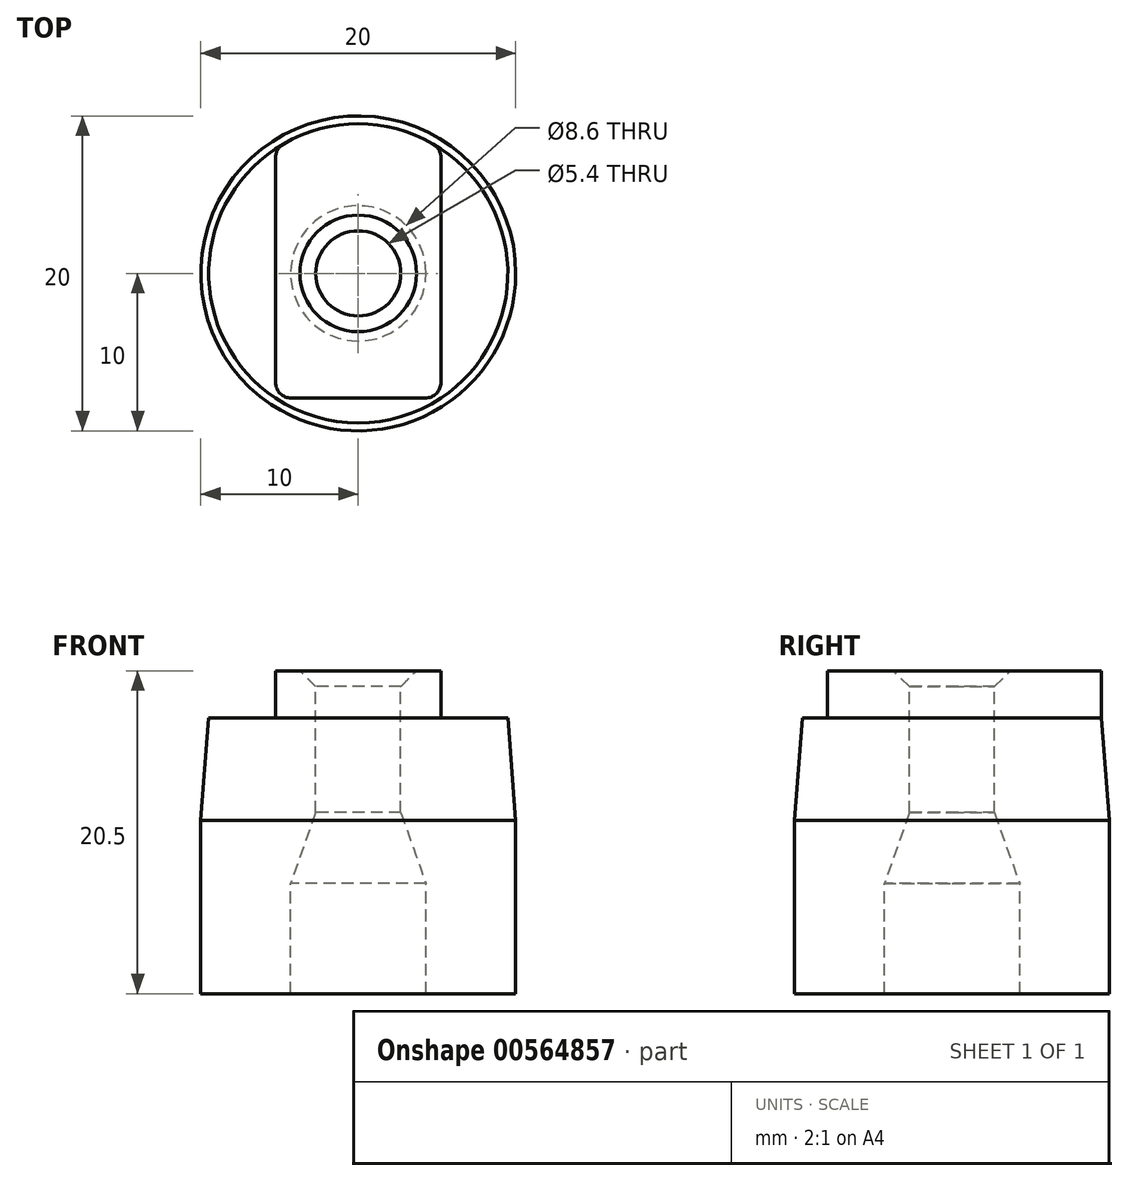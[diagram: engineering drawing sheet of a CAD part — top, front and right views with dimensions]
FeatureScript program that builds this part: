
annotation { "Feature Type Name" : "Feature", "Feature Type Description" : "" }
export const myFeature = defineFeature(function(context is Context, id is Id, definition is map)
    precondition{}
    {
        {
            var Q0;
            Q0=qCreatedBy(makeId("Front.planeOp"),FACE);
            var sketch = newSketch(context, id + "F0", { "sketchPlane" : qUnion([Q0])});
            skLineSegment(sketch, "E0", {"start": v(4.3, 0) * mm, "end": v(10, 0) * mm});
            skLineSegment(sketch, "E1", {"start": v(10, 0) * mm, "end": v(10, 11) * mm});
            skLineSegment(sketch, "E2", {"start": v(10, 11) * mm, "end": v(9.5, 17.5) * mm});
            skLineSegment(sketch, "E3", {"start": v(9.5, 17.5) * mm, "end": v(2.7, 17.5) * mm});
            skLineSegment(sketch, "E4", {"start": v(2.7, 17.5) * mm, "end": v(2.7, 11.5) * mm});
            skLineSegment(sketch, "E5", {"start": v(2.7, 11.5) * mm, "end": v(4.3, 7) * mm});
            skLineSegment(sketch, "E6", {"start": v(4.3, 7) * mm, "end": v(4.3, 0) * mm});
            skSolve(sketch);
        }
        {
            var Q0;
            Q0=qCreatedBy(makeId("Front.planeOp"),FACE);
            var sketch = newSketch(context, id + "F1", { "sketchPlane" : qUnion([Q0])});
            skLineSegment(sketch, "E7", {"start": v(0, 48.35) * mm, "end": v(0, -22.75) * mm});
            skSolve(sketch);
        }
        {
            var Q0;
            Q0=qSketchRegion(id+"F0",true);
            var Q1;
            Q1=sQuery(id+"F1.wireOp",EDGE,"E7");
            revolve(context, id + "F2", {"entities" : qUnion([Q0]), "axis" : qUnion([Q1]), "revolveType" : RevolveType.FULL});
        }
        {
            var Q0;
            Q0=makeQuery(id+"F2.opRevolve","SWEPT_FACE",FACE,{"disambiguationData":[OSD([sQuery(id+"F0.wireOp",EDGE,"E3")])]});
            var sketch = newSketch(context, id + "F3", { "sketchPlane" : qUnion([Q0])});
            skLineSegment(sketch, "E8.bottom", {"start": v(5.25, 7.92) * mm, "end": v(-5.25, 7.92) * mm});
            skLineSegment(sketch, "E8.top", {"start": v(5.25, -7.92) * mm, "end": v(-5.25, -7.92) * mm});
            skLineSegment(sketch, "E8.left", {"start": v(5.25, 7.92) * mm, "end": v(5.25, -7.92) * mm});
            skLineSegment(sketch, "E8.right", {"start": v(-5.25, 7.92) * mm, "end": v(-5.25, -7.92) * mm});
            skPoint(sketch, "E8.middle", {"position": v(0, 0) * mm});
            skSolve(sketch);
        }
        {
            var Q0;
            Q0=makeQuery(id+"F3.imprint","IMPRINT",FACE,{"disambiguationData":[TD([[makeQuery(id+"F3.imprint","IMPRINT",EDGE,{"derivedFrom":sQuery(id+"F3.wireOp",EDGE,"E8.bottom")}),1.0]])]});
            extrude(context, id + "F4", {"entities" : qUnion([Q0]), "operationType" : NewBodyOperationType.ADD, "depth" : 3 * mm});
        }
        {
            var Q0;
            Q0=makeQuery(id+"F4.opExtrude","SWEPT_EDGE",EDGE,{"disambiguationData":[OSD([sQuery(id+"F3.wireOp",EDGE,"E8.top"),sQuery(id+"F3.wireOp",EDGE,"E8.right")])]});
            var Q1;
            Q1=makeQuery(id+"F4.opExtrude","SWEPT_EDGE",EDGE,{"disambiguationData":[OSD([sQuery(id+"F3.wireOp",EDGE,"E8.top"),sQuery(id+"F3.wireOp",EDGE,"E8.left")])]});
            fillet(context, id + "F5", {"entities" : qUnion([Q0, Q1]), "radius" : 1 * mm, "allowEdgeOverflow" : false});
        }
        {
            var Q0;
            {var subQ0=makeQuery(id+"F2.opRevolve","SWEPT_FACE",FACE,{"disambiguationData":[OSD([sQuery(id+"F0.wireOp",EDGE,"E3")])]});Q0=makeQuery(id+"F4.boolean.opBoolean","SPLIT",FACE,{"disambiguationData":[TD([makeQuery(id+"F2.opRevolve","SWEPT_FACE",FACE,{"disambiguationData":[OSD([sQuery(id+"F0.wireOp",EDGE,"E2")])]}),subQ0,makeQuery(id+"F4.opExtrude","SWEPT_FACE",FACE,{"disambiguationData":[OSD([sQuery(id+"F3.wireOp",EDGE,"E8.bottom")])]}),makeQuery(id+"F4.opExtrude","SWEPT_FACE",FACE,{"disambiguationData":[OSD([sQuery(id+"F3.wireOp",EDGE,"E8.left")])]}),makeQuery(id+"F4.opExtrude","SWEPT_FACE",FACE,{"disambiguationData":[OSD([sQuery(id+"F3.wireOp",EDGE,"E8.right")])]})])],"derivedFrom":subQ0});}
            var sketch = newSketch(context, id + "F6", { "sketchPlane" : qUnion([Q0])});
            skLineSegment(sketch, "E9", {"start": v(5.25, 7.92) * mm, "end": v(-5.25, 7.92) * mm});
            skArc(sketch, "E10", {"start": v(5.25, 7.92) * mm, "mid": v(0, 9.5) * mm, "end": v(-5.25, 7.92) * mm});
            skSolve(sketch);
        }
        {
            var Q0;
            Q0=qSketchRegion(id+"F6",true);
            extrude(context, id + "F7", {"entities" : qUnion([Q0]), "operationType" : NewBodyOperationType.ADD, "depth" : 3 * mm});
        }
        {
            var Q0;
            {var subQ0=sQuery(id+"F6.wireOp",EDGE,"E10");var subQ1=sQuery(id+"F6.wireOp",EDGE,"E9");var subQ2=sQuery(id+"F0.wireOp",EDGE,"E3");var subQ3=sQuery(id+"F0.wireOp",EDGE,"E2");Q0=makeQuery(id+"F7.boolean.opBoolean","MERGE",EDGE,{"derivedFrom":[makeQuery(id+"F4.opExtrude","SWEPT_EDGE",EDGE,{"disambiguationData":[OSD([subQ3,subQ2,sQuery(id+"F3.wireOp",EDGE,"E8.bottom"),sQuery(id+"F3.wireOp",EDGE,"E8.right")])]}),makeQuery(id+"F7.opExtrude","SWEPT_EDGE",EDGE,{"disambiguationData":[OSD([subQ3,subQ2,subQ1,subQ0]),TDD([makeQuery(id+"F6.imprint","INTERSECT",VERTEX,{"disambiguationData":[OD(1.0)],"derivedFrom":[makeQuery(id+"F4.boolean.opBoolean","SPLIT",EDGE,{"disambiguationData":[OD(0.0)],"derivedFrom":makeQuery(id+"F2.opRevolve","SWEPT_EDGE",EDGE,{"disambiguationData":[OSD([subQ3,subQ2])]})}),subQ1,subQ0]})])]})]});}
            var Q1;
            {var subQ0=sQuery(id+"F6.wireOp",EDGE,"E10");var subQ1=sQuery(id+"F6.wireOp",EDGE,"E9");var subQ2=sQuery(id+"F0.wireOp",EDGE,"E3");var subQ3=sQuery(id+"F0.wireOp",EDGE,"E2");Q1=makeQuery(id+"F7.boolean.opBoolean","MERGE",EDGE,{"derivedFrom":[makeQuery(id+"F4.opExtrude","SWEPT_EDGE",EDGE,{"disambiguationData":[OSD([subQ3,subQ2,sQuery(id+"F3.wireOp",EDGE,"E8.bottom"),sQuery(id+"F3.wireOp",EDGE,"E8.left")])]}),makeQuery(id+"F7.opExtrude","SWEPT_EDGE",EDGE,{"disambiguationData":[OSD([subQ3,subQ2,subQ1,subQ0]),TDD([makeQuery(id+"F6.imprint","INTERSECT",VERTEX,{"disambiguationData":[OD(0.0)],"derivedFrom":[makeQuery(id+"F4.boolean.opBoolean","SPLIT",EDGE,{"disambiguationData":[OD(0.0)],"derivedFrom":makeQuery(id+"F2.opRevolve","SWEPT_EDGE",EDGE,{"disambiguationData":[OSD([subQ3,subQ2])]})}),subQ1,subQ0]})])]})]});}
            fillet(context, id + "F8", {"entities" : qUnion([Q0, Q1]), "radius" : 1 * mm, "tangentPropagation" : true, "allowEdgeOverflow" : false});
        }
        {
            var Q0;
            Q0=makeQuery(id+"F4.opExtrude","CAP_EDGE",EDGE,{"disambiguationData":[OSD([sQuery(id+"F0.wireOp",EDGE,"E3"),sQuery(id+"F0.wireOp",EDGE,"E4")])],"isStart":false});
            chamfer(context, id + "F9", {"entities" : qUnion([Q0]), "width" : 1 * mm, "tangentPropagation" : true});
        }
    });
